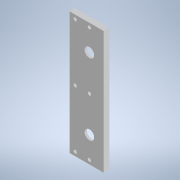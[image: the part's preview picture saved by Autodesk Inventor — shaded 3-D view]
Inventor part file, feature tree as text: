
AUTODESK INVENTOR PART (.ipt)
format: ipt  version: 2021 (Build 250183000, 183)  size: 268,800 bytes
history: native  units: in
note: dims shown in document units (in); Inventor stores cm internally (conversion verified against a paired STEP export)
features: reference x30, extrude x10, sketch x9, other x8, plane x1
ambient origin geometry x8: Origin, YZ Plane, XZ Plane, XY Plane, X Axis, Y Axis, Z Axis, Center Point
bodies: Solid1 (feature_tree)
feature tree (58):
  plane  "Work Plane1"
  extrude  "Extrusion1"  Depth=0.0787in
  extrude  "Extrusion2"  Depth=0.0079in
  extrude  "Extrusion3"  Depth=0.0079in
  extrude  "Extrusion4"  Depth=0.0079in
  extrude  "Extrusion5"  TaperAngle=0.0deg  [1 undecoded]
  sketch  "Sketch6"  dims[d12=0.1201in d13=0.0in d14=0.1201in d15=0.0in]
  extrude  "Extrusion6"  Depth=0.1201in TaperAngle=0.0deg
  extrude  "Extrusion7"  Depth=0.1201in
  extrude  "Extrusion8"  Depth=0.1142in
  extrude  "Extrusion9"  Depth=0.3937in
  extrude  "Extrusion10"  TaperAngle=0.0deg  [1 undecoded]
  sketch  "Sketch1"  dims[d0=0.0787in d1=0.0in d2=0.0079in]
  reference  "Reference1"
  reference  "Reference2"
  reference  "Reference3"
  reference  "Reference4"
  reference  "Reference5"
  reference  "Reference6"
  reference  "Reference7"
  reference  "Reference8"
  reference  "Reference9"
  reference  "Reference10"
  reference  "Reference11"
  sketch  "Sketch2"  dims[d3=0.0079in d4=0.0079in]
  reference  "Reference12"
  reference  "Reference13"
  reference  "Reference14"
  reference  "Reference15"
  reference  "Reference16"
  reference  "Reference17"
  reference  "Reference18"
  reference  "Reference19"
  sketch  "Sketch3"  dims[d5=0.0079in d6=0.0079in]
  reference  "Reference20"
  sketch  "Sketch4"  dims[d7=0.0079in d8=0.0079in]
  reference  "Reference23"
  sketch  "Sketch5"  dims[d9=0.0079in d10=0.0in d11=0.0in]
  reference  "Reference24"
  reference  "Reference25"
  reference  "Reference26"
  reference  "Reference27"
  reference  "Reference28"
  reference  "Reference29"
  reference  "Reference30"
  reference  "Reference31"
  sketch  "Sketch7"  dims[d16=0.1201in d17=0.0in d18=0.8169in]
  sketch  "Sketch8"  dims[d19=0.1142in d20=0.1142in]
  sketch  "Sketch9"  dims[d21=0.2362in d22=0.2362in d23=0.0in d24=0.0in d25=0.3937in d26=0.0in d27=0.3937in d28=0.0in d29=0.063in d30=0.063in d31=0.063in d32=0.063in d33=0.063in d34=0.063in d35=0.063in d36=0.063in d37=0.0394in d38=0.0in d39=0.3937in d40=0.0in]
  reference  "Reference32"
  parser-record x2  (decoder bookkeeping rows leaked as tree rows — omitted from the tree; the rows remain in map.json)
  other  "assembly.iam"
  other  "pi_cam_stereo_case:1"
  other  "RspCameraMia:3"
  other  "OVA5647_Housing:1"
  other  "RspCameraMia:2"
  other  "PicameraPCB:1"
note: 2 required parameter values undecoded (feature->parameter linkage not recoverable at this tier; creation-order binding heuristic only, values carry confidence <= 0.55)
note: 2 file-system paths scrubbed to <path> (originals preserved in map.json)
